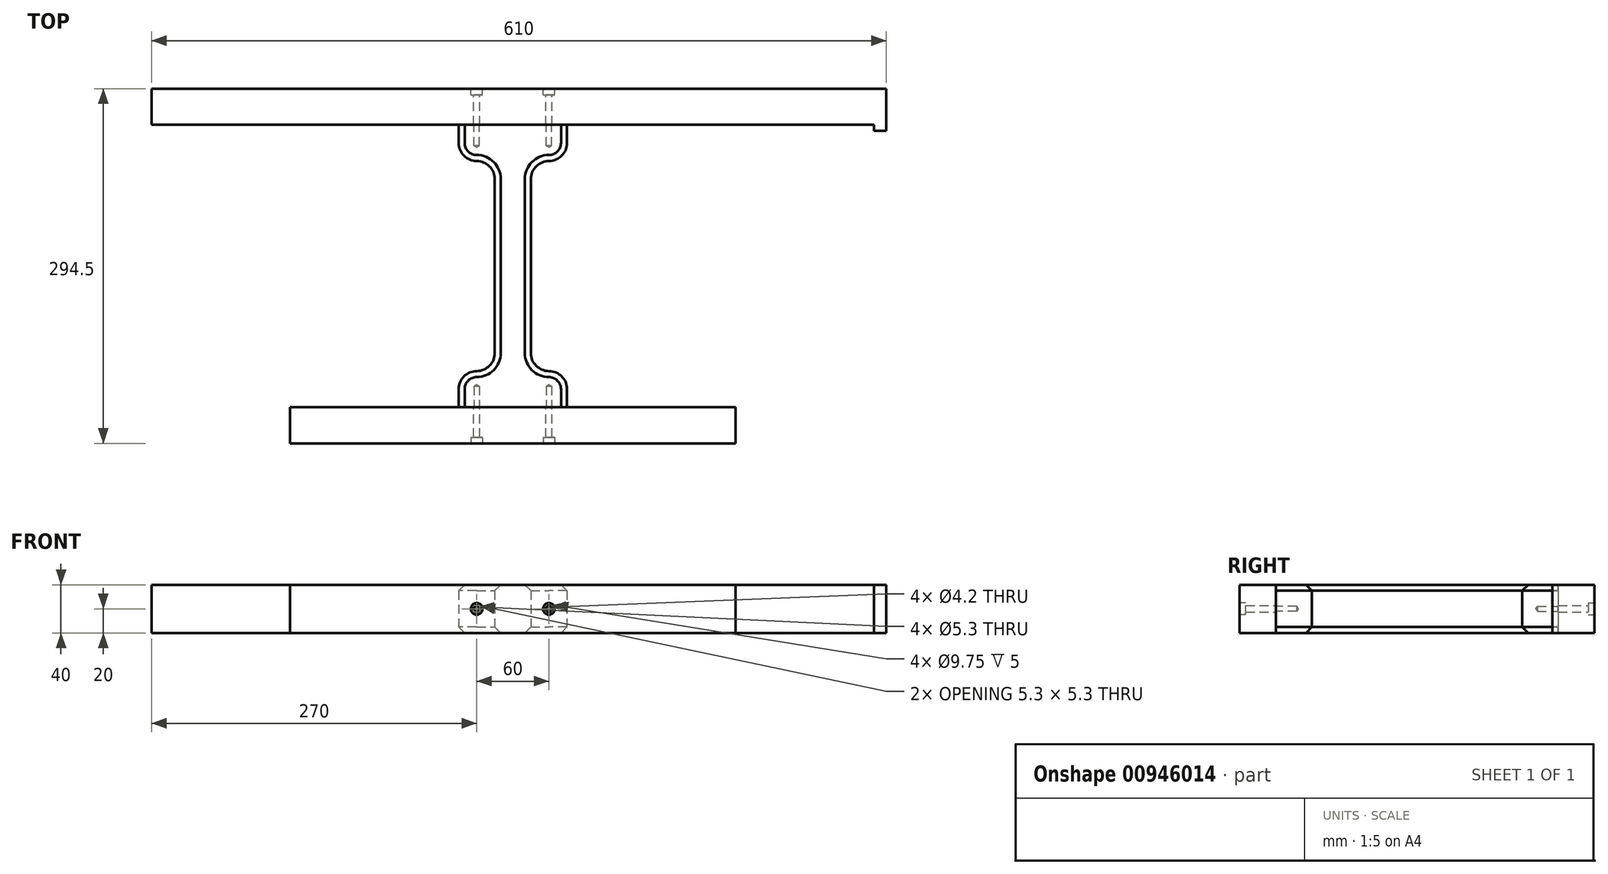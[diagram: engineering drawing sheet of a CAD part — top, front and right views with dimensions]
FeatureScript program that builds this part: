
annotation { "Feature Type Name" : "Feature", "Feature Type Description" : "" }
export const myFeature = defineFeature(function(context is Context, id is Id, definition is map)
    precondition{}
    {
        {
            var Q0;
            Q0=qCreatedBy(makeId("Top.planeOp"),FACE);
            var sketch = newSketch(context, id + "F0", { "sketchPlane" : qUnion([Q0])});
            skLineSegment(sketch, "E0", {"start": v(-300, 294.5) * mm, "end": v(300, 294.5) * mm});
            skLineSegment(sketch, "E1", {"start": v(300, 294.5) * mm, "end": v(300, 264.5) * mm});
            skLineSegment(sketch, "E2", {"start": v(300, 264.5) * mm, "end": v(15, 264.5) * mm});
            skLineSegment(sketch, "E3", {"start": v(15, 264.5) * mm, "end": v(15, 30) * mm});
            skLineSegment(sketch, "E4", {"start": v(15, 30) * mm, "end": v(185, 30) * mm});
            skLineSegment(sketch, "E5", {"start": v(185, 30) * mm, "end": v(185, 0) * mm});
            skLineSegment(sketch, "E6", {"start": v(185, 0) * mm, "end": v(-185, 0) * mm});
            skLineSegment(sketch, "E7", {"start": v(-185, 0) * mm, "end": v(-185, 30) * mm});
            skLineSegment(sketch, "E8", {"start": v(-185, 30) * mm, "end": v(-15, 30) * mm});
            skLineSegment(sketch, "E9", {"start": v(-15, 30) * mm, "end": v(-15, 264.5) * mm});
            skLineSegment(sketch, "E10", {"start": v(-15, 264.5) * mm, "end": v(-300, 264.5) * mm});
            skLineSegment(sketch, "E11", {"start": v(-300, 264.5) * mm, "end": v(-300, 294.5) * mm});
            skLineSegment(sketch, "E12.bottom", {"start": v(300, 294.5) * mm, "end": v(310, 294.5) * mm});
            skLineSegment(sketch, "E12.top", {"start": v(300, 259.5) * mm, "end": v(310, 259.5) * mm});
            skLineSegment(sketch, "E12.left", {"start": v(300, 294.5) * mm, "end": v(300, 259.5) * mm});
            skLineSegment(sketch, "E12.right", {"start": v(310, 294.5) * mm, "end": v(310, 259.5) * mm});
            skLineSegment(sketch, "E13", {"start": v(-15, 264.5) * mm, "end": v(15, 264.5) * mm});
            skLineSegment(sketch, "E14", {"start": v(-15, 30) * mm, "end": v(15, 30) * mm});
            skLineSegment(sketch, "E15", {"start": v(-45, 264.5) * mm, "end": v(-45, 234.5) * mm});
            skLineSegment(sketch, "E16", {"start": v(-45, 234.5) * mm, "end": v(-15, 234.5) * mm});
            skLineSegment(sketch, "E17", {"start": v(15, 234.5) * mm, "end": v(45, 234.5) * mm});
            skLineSegment(sketch, "E18", {"start": v(45, 234.5) * mm, "end": v(45, 264.5) * mm});
            skLineSegment(sketch, "E19", {"start": v(15, 60) * mm, "end": v(45, 60) * mm});
            skLineSegment(sketch, "E20", {"start": v(45, 60) * mm, "end": v(45, 30) * mm});
            skLineSegment(sketch, "E21", {"start": v(-15, 60) * mm, "end": v(-45, 60) * mm});
            skLineSegment(sketch, "E22", {"start": v(-45, 60) * mm, "end": v(-45, 30) * mm});
            skSolve(sketch);
        }
        {
            var Q0;
            Q0=makeQuery(id+"F0.imprint","IMPRINT",FACE,{"disambiguationData":[TD([[makeQuery(id+"F0.imprint","IMPRINT",EDGE,{"derivedFrom":sQuery(id+"F0.wireOp",EDGE,"E0")}),-1.0]])]});
            var Q1;
            {var subQ3=sQuery(id+"F0.wireOp",EDGE,"E12.bottom");Q1=makeQuery(id+"F0.imprint","IMPRINT",FACE,{"disambiguationData":[TD([[makeQuery(id+"F0.imprint","IMPRINT",EDGE,{"derivedFrom":subQ3}),-1.0]])]});}
            extrude(context, id + "F1", {"entities" : qUnion([Q0, Q1]), "depth" : 40 * mm, "offsetDistance" : 25 * mm});
        }
        {
            var Q0;
            Q0=makeQuery(id+"F0.imprint","IMPRINT",FACE,{"disambiguationData":[TD([[makeQuery(id+"F0.imprint","IMPRINT",EDGE,{"derivedFrom":sQuery(id+"F0.wireOp",EDGE,"E3")}),-1.0]])]});
            var Q1;
            {var subQ4=sQuery(id+"F0.wireOp",EDGE,"E15");Q1=makeQuery(id+"F0.imprint","IMPRINT",FACE,{"disambiguationData":[TD([[makeQuery(id+"F0.imprint","IMPRINT",EDGE,{"derivedFrom":subQ4}),1.0]])]});}
            var Q2;
            {var subQ4=sQuery(id+"F0.wireOp",EDGE,"E17");Q2=makeQuery(id+"F0.imprint","IMPRINT",FACE,{"disambiguationData":[TD([[makeQuery(id+"F0.imprint","IMPRINT",EDGE,{"derivedFrom":subQ4}),1.0]])]});}
            var Q3;
            {var subQ4=sQuery(id+"F0.wireOp",EDGE,"E21");Q3=makeQuery(id+"F0.imprint","IMPRINT",FACE,{"disambiguationData":[TD([[makeQuery(id+"F0.imprint","IMPRINT",EDGE,{"derivedFrom":subQ4}),1.0]])]});}
            var Q4;
            {var subQ3=sQuery(id+"F0.wireOp",EDGE,"E19");Q4=makeQuery(id+"F0.imprint","IMPRINT",FACE,{"disambiguationData":[TD([[makeQuery(id+"F0.imprint","IMPRINT",EDGE,{"derivedFrom":subQ3}),-1.0]])]});}
            extrude(context, id + "F2", {"entities" : qUnion([Q0, Q1, Q2, Q3, Q4]), "depth" : 40 * mm, "offsetDistance" : 25 * mm});
        }
        {
            var Q0;
            Q0=makeQuery(id+"F0.imprint","IMPRINT",FACE,{"disambiguationData":[TD([[makeQuery(id+"F0.imprint","IMPRINT",EDGE,{"derivedFrom":sQuery(id+"F0.wireOp",EDGE,"E4")}),-1.0]])]});
            extrude(context, id + "F3", {"entities" : qUnion([Q0]), "depth" : 40 * mm, "offsetDistance" : 25 * mm});
        }
        {
            var Q0;
            Q0=makeQuery(id+"F2.opExtrude","SWEPT_EDGE",EDGE,{"disambiguationData":[OSD([sQuery(id+"F0.wireOp",EDGE,"E17"),sQuery(id+"F0.wireOp",EDGE,"E18")])]});
            var Q1;
            Q1=makeQuery(id+"F2.opExtrude","SWEPT_EDGE",EDGE,{"disambiguationData":[OSD([sQuery(id+"F0.wireOp",EDGE,"E15"),sQuery(id+"F0.wireOp",EDGE,"E16")])]});
            var Q2;
            Q2=makeQuery(id+"F2.opExtrude","SWEPT_EDGE",EDGE,{"disambiguationData":[OSD([sQuery(id+"F0.wireOp",EDGE,"E21"),sQuery(id+"F0.wireOp",EDGE,"E22")])]});
            var Q3;
            Q3=makeQuery(id+"F2.opExtrude","SWEPT_EDGE",EDGE,{"disambiguationData":[OSD([sQuery(id+"F0.wireOp",EDGE,"E19"),sQuery(id+"F0.wireOp",EDGE,"E20")])]});
            var Q4;
            Q4=makeQuery(id+"F2.opExtrude","SWEPT_EDGE",EDGE,{"disambiguationData":[OSD([sQuery(id+"F0.wireOp",EDGE,"E3"),sQuery(id+"F0.wireOp",EDGE,"E17")])]});
            var Q5;
            Q5=makeQuery(id+"F2.opExtrude","SWEPT_EDGE",EDGE,{"disambiguationData":[OSD([sQuery(id+"F0.wireOp",EDGE,"E9"),sQuery(id+"F0.wireOp",EDGE,"E16")])]});
            var Q6;
            Q6=makeQuery(id+"F2.opExtrude","SWEPT_EDGE",EDGE,{"disambiguationData":[OSD([sQuery(id+"F0.wireOp",EDGE,"E9"),sQuery(id+"F0.wireOp",EDGE,"E21")])]});
            var Q7;
            Q7=makeQuery(id+"F2.opExtrude","SWEPT_EDGE",EDGE,{"disambiguationData":[OSD([sQuery(id+"F0.wireOp",EDGE,"E3"),sQuery(id+"F0.wireOp",EDGE,"E19")])]});
            fillet(context, id + "F4", {"entities" : qUnion([Q0, Q1, Q2, Q3, Q4, Q5, Q6, Q7]), "radius" : 15 * mm, "tangentPropagation" : true, "allowEdgeOverflow" : false});
        }
        {
            var Q0;
            Q0=makeQuery(id+"F2.opExtrude","CAP_EDGE",EDGE,{"disambiguationData":[OSD([sQuery(id+"F0.wireOp",EDGE,"E9")])],"isStart":false});
            var Q1;
            Q1=makeQuery(id+"F2.opExtrude","CAP_EDGE",EDGE,{"disambiguationData":[OSD([sQuery(id+"F0.wireOp",EDGE,"E3")])],"isStart":false});
            var Q2;
            Q2=makeQuery(id+"F2.opExtrude","CAP_EDGE",EDGE,{"disambiguationData":[OSD([sQuery(id+"F0.wireOp",EDGE,"E9")])],"isStart":true});
            var Q3;
            Q3=makeQuery(id+"F2.opExtrude","CAP_EDGE",EDGE,{"disambiguationData":[OSD([sQuery(id+"F0.wireOp",EDGE,"E3")])],"isStart":true});
            chamfer(context, id + "F5", {"entities" : qUnion([Q0, Q1, Q2, Q3]), "width" : 5 * mm, "tangentPropagation" : true});
        }
        {
            var Q0;
            Q0=makeQuery(id+"F1.opExtrude","SWEPT_FACE",FACE,{"disambiguationData":[OSD([sQuery(id+"F0.wireOp",EDGE,"E0"),sQuery(id+"F0.wireOp",EDGE,"E12.bottom")])]});
            var sketch = newSketch(context, id + "F6", { "sketchPlane" : qUnion([Q0])});
            skPoint(sketch, "E23.0", {"position": v(-30, 20) * mm});
            skPoint(sketch, "E24.0", {"position": v(30, 20) * mm});
            skSolve(sketch);
        }
        {
            var Q0;
            Q0=makeQuery(id+"F3.opExtrude","SWEPT_FACE",FACE,{"disambiguationData":[OSD([sQuery(id+"F0.wireOp",EDGE,"E6")])]});
            var sketch = newSketch(context, id + "F7", { "sketchPlane" : qUnion([Q0])});
            skPoint(sketch, "E25.0", {"position": v(-30, 20) * mm});
            skPoint(sketch, "E26.0", {"position": v(30, 20) * mm});
            skSolve(sketch);
        }
        {
            var Q0;
            Q0=sQuery(id+"F6.wireOp",VERTEX,"E23.0");
            var Q1;
            Q1=sQuery(id+"F6.wireOp",VERTEX,"E24.0");
            var Q2;
            Q2=sQuery(id+"F7.wireOp",VERTEX,"E25.0");
            var Q3;
            Q3=sQuery(id+"F7.wireOp",VERTEX,"E26.0");
            var Q4;
            Q4=makeQuery(id+"F1.opExtrude","SWEPT_BODY",BODY,{"disambiguationData":[OSD([sQuery(id+"F0.wireOp",EDGE,"E0"),sQuery(id+"F0.wireOp",EDGE,"E2"),sQuery(id+"F0.wireOp",EDGE,"E10"),sQuery(id+"F0.wireOp",EDGE,"E11"),sQuery(id+"F0.wireOp",EDGE,"E12.bottom"),sQuery(id+"F0.wireOp",EDGE,"E12.top"),sQuery(id+"F0.wireOp",EDGE,"E12.left"),sQuery(id+"F0.wireOp",EDGE,"E12.right"),sQuery(id+"F0.wireOp",EDGE,"E13")])]});
            var Q5;
            Q5=makeQuery(id+"F3.opExtrude","SWEPT_BODY",BODY,{"disambiguationData":[OSD([sQuery(id+"F0.wireOp",EDGE,"E4"),sQuery(id+"F0.wireOp",EDGE,"E5"),sQuery(id+"F0.wireOp",EDGE,"E6"),sQuery(id+"F0.wireOp",EDGE,"E7"),sQuery(id+"F0.wireOp",EDGE,"E8"),sQuery(id+"F0.wireOp",EDGE,"E14")])]});
            hole(context, id + "F8", {"style" : HoleStyle.C_BORE, "endStyle" : HoleEndStyle.THROUGH, "standardTappedOrClearance" : lookupTablePath({ "fit" : "Close", "standard" : "ISO", "size" : "M5", "type" : "Clearance" }), "standardBlindInLast" : lookupTablePath({ "fit" : "Close", "standard" : "ISO", "engagement" : "75%", "pitch" : "0.8 mm", "size" : "M5", "type" : "Clearance & tapped" }), "holeDiameter" : 5.3 * mm, "cBoreDiameter" : 9.75 * mm, "cBoreDepth" : 5 * mm, "majorDiameter" : 5 * mm, "tappedDepth" : 15 * mm, "tapClearance" : 3, "startFromSketch" : true, "locations" : qUnion([Q0, Q1, Q2, Q3]), "scope" : qUnion([Q4, Q5])});
        }
        {
            var Q0;
            Q0=sQuery(id+"F6.wireOp",VERTEX,"E24.0");
            var Q1;
            Q1=sQuery(id+"F6.wireOp",VERTEX,"E23.0");
            var Q2;
            Q2=sQuery(id+"F7.wireOp",VERTEX,"E25.0");
            var Q3;
            Q3=sQuery(id+"F7.wireOp",VERTEX,"E26.0");
            var Q4;
            Q4=makeQuery(id+"F2.opExtrude","SWEPT_BODY",BODY,{"disambiguationData":[OSD([sQuery(id+"F0.wireOp",EDGE,"E2"),sQuery(id+"F0.wireOp",EDGE,"E3"),sQuery(id+"F0.wireOp",EDGE,"E4"),sQuery(id+"F0.wireOp",EDGE,"E8"),sQuery(id+"F0.wireOp",EDGE,"E9"),sQuery(id+"F0.wireOp",EDGE,"E10"),sQuery(id+"F0.wireOp",EDGE,"E13"),sQuery(id+"F0.wireOp",EDGE,"E14"),sQuery(id+"F0.wireOp",EDGE,"E15"),sQuery(id+"F0.wireOp",EDGE,"E16"),sQuery(id+"F0.wireOp",EDGE,"E17"),sQuery(id+"F0.wireOp",EDGE,"E18"),sQuery(id+"F0.wireOp",EDGE,"E19"),sQuery(id+"F0.wireOp",EDGE,"E20"),sQuery(id+"F0.wireOp",EDGE,"E21"),sQuery(id+"F0.wireOp",EDGE,"E22")])]});
            hole(context, id + "F9", {"style" : HoleStyle.SIMPLE, "endStyle" : HoleEndStyle.BLIND, "standardTappedOrClearance" : lookupTablePath({ "standard" : "ISO", "engagement" : "75%", "pitch" : "0.8 mm", "size" : "M5", "type" : "Tapped" }), "standardBlindInLast" : lookupTablePath({ "standard" : "ISO", "fit" : "Normal", "engagement" : "75%", "pitch" : "0.8 mm", "size" : "M5", "type" : "Clearance & tapped" }), "holeDiameter" : 4.2 * mm, "majorDiameter" : 5 * mm, "showTappedDepth" : true, "holeDepth" : 17.4 * mm, "tappedDepth" : 15 * mm, "tapClearance" : 3, "locations" : qUnion([Q0, Q1, Q2, Q3]), "scope" : qUnion([Q4])});
        }
    });
